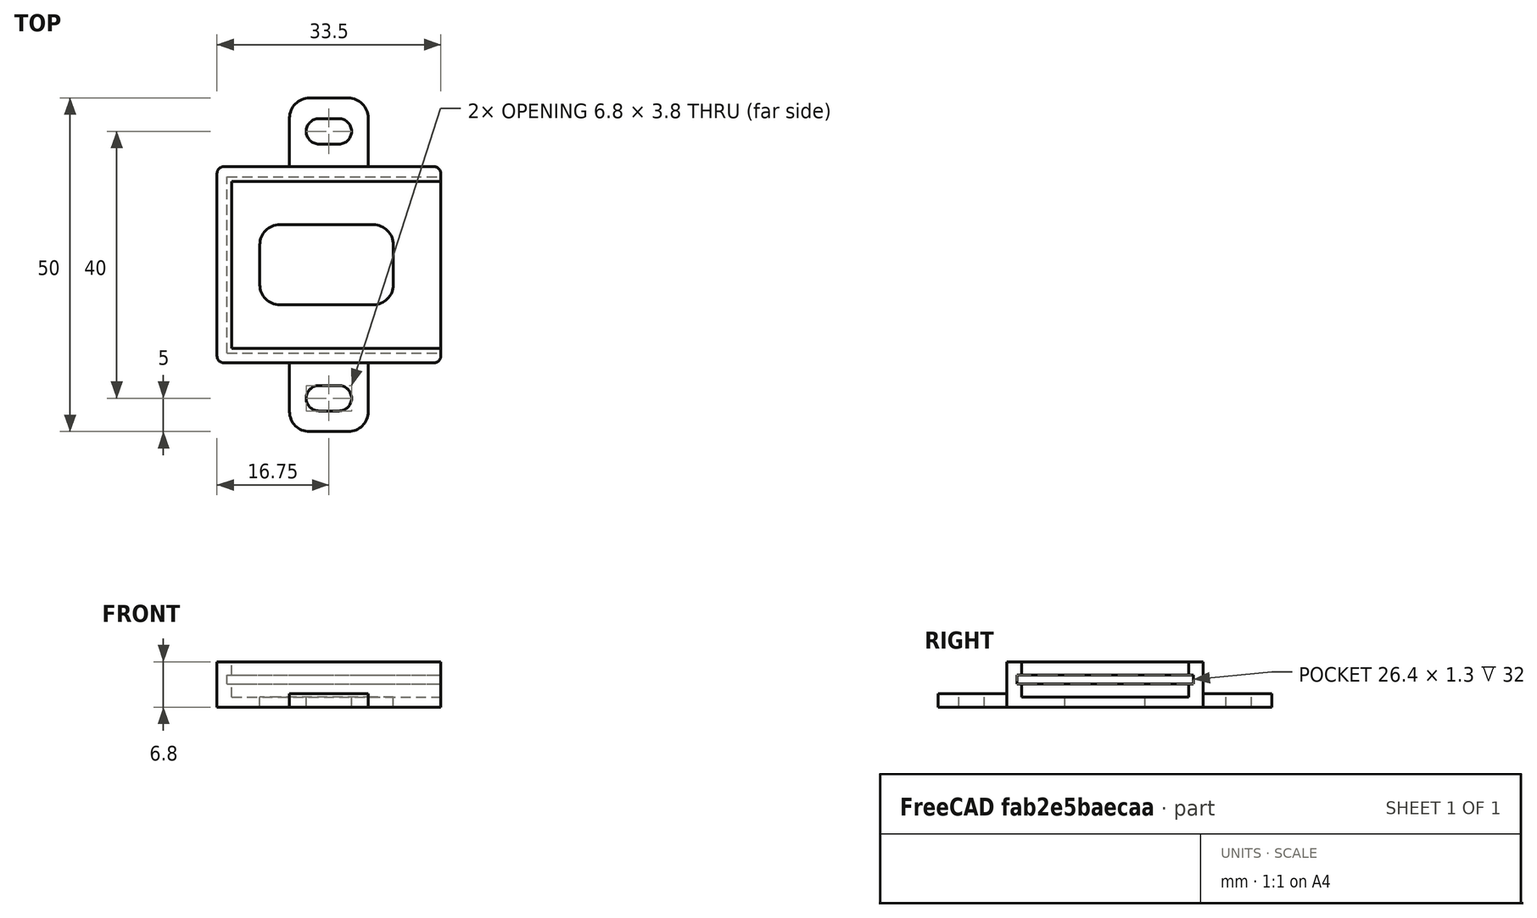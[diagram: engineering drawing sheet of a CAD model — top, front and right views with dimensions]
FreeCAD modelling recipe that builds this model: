
FCSTD DOCUMENT  (FreeCAD 0.19R23578 (Git))
Label: ir_sensor_cheapduino
License: FreeArt
LicenseURL: http://artlibre.org/licence/lal
objects: Part::Box×4, Part::Fillet×2, Part::MultiFuse×2, Spreadsheet::Sheet×1, Part::Feature×1, Part::Cut×1, App::Part×1
note: 10 computed .brp shape members not serialized (recipe doc carries the construction recipe); baked Part::Feature solids carry a one-line shape summary decoded from their .brp

FEATURE [Spreadsheet::Sheet] Spreadsheet  label="p"
  cells = A1=pcb_x; B1(pcb_x)=32; A2=pcb_y; B2(pcb_y)=26.4; A3=pcb_z; B3(pcb_z)=1.3; A4=pcb_under; B4(pcb_under)=2; A5=side_wall; B5(side_wall)=1.5; A6=pcb_side_lane; B6(pcb_side_lane)=0.7; A7=bottom_wall; B7(bottom_wall)=1.5; A8=pcb_above; B8(pcb_above)=2; A9=bottom_hole_x; B9(bottom_hole_x)=20; A10=bottom_hole_y; B10(bottom_hole_y)=12
FEATURE [Part::Box] Box  label="external cube"
  AttacherType = Attacher::AttachEngine3D
  Height = 6.8
  Length = 33.5
  Width = 29.4
  expr: Length = <<p>>.pcb_x + <<p>>.side_wall
  expr: Width = <<p>>.pcb_y + 2 * <<p>>.side_wall
  expr: Height = <<p>>.bottom_wall + <<p>>.pcb_under + <<p>>.pcb_z + <<p>>.pcb_above
FEATURE [Part::Box] Box006  label="internal cube"
  AttacherType = Attacher::AttachEngine3D
  Height = 5.3
  Length = 32.1
  Placement = pos=(2.2,2.2,1.5) rot=(0,0,1;0rad)
  Width = 25
  expr: Length = <<p>>.pcb_x - 2 * <<p>>.pcb_side_lane + <<p>>.side_wall
  expr: Width = <<p>>.pcb_y - 2 * <<p>>.pcb_side_lane
  expr: Height = <<p>>.pcb_under + <<p>>.pcb_z + <<p>>.pcb_above
  expr: .Placement.Base.z = <<p>>.bottom_wall
  expr: .Placement.Base.x = <<p>>.side_wall + <<p>>.pcb_side_lane
  expr: .Placement.Base.y = <<p>>.side_wall + <<p>>.pcb_side_lane
FEATURE [Part::Box] Box007  label="pcb extract cube"
  AttacherType = Attacher::AttachEngine3D
  Height = 1.3
  Length = 32
  Placement = pos=(1.5,1.5,3.5) rot=(0,0,1;0rad)
  Width = 26.4
  expr: Height = <<p>>.pcb_z
  expr: .Placement.Base.z = <<p>>.bottom_wall + <<p>>.pcb_under
  expr: Width = <<p>>.pcb_y
  expr: Length = <<p>>.pcb_x
  expr: .Placement.Base.x = <<p>>.side_wall
  expr: .Placement.Base.y = <<p>>.side_wall
FEATURE [Part::Fillet] Fillet  label="external fillet"
  Base = -> Box
  Edges = 4 edges r=1: [Edge1,Edge3,Edge5,Edge7]
FEATURE [Part::Box] Box008  label="bottom hole"
  AttacherType = Attacher::AttachEngine3D
  Height = 10
  Length = 20
  Placement = pos=(6.4,8.7,0) rot=(0,0,1;0rad)
  Width = 12
  expr: .Placement.Base.y = (<<p>>.pcb_y + 2 * <<p>>.side_wall - <<p>>.bottom_hole_y) / 2
  expr: .Placement.Base.x = (<<p>>.pcb_x + <<p>>.side_wall - <<p>>.pcb_side_lane - <<p>>.bottom_hole_x) / 2
  expr: Width = <<p>>.bottom_hole_y
  expr: Length = <<p>>.bottom_hole_x
FEATURE [Part::Fillet] Fillet001  label="bottom hole fillet"
  Base = -> Box008
  Edges = 4 edges r=3: [Edge1,Edge3,Edge5,Edge7]
FEATURE [Part::MultiFuse] Fusion  label="extract fusion"
  Shapes = -> [Box006,Box007,Fillet001]
FEATURE [Part::Feature] Cut002001  label="attach plane y dir001"
  Placement = pos=(10.85,-10.3,0) rot=(0,0,1;0rad)
  shape: bbox 11.8 x 50 x 2 mm, 20 faces (baked)
FEATURE [Part::MultiFuse] Fusion001  label="solid fusion"
  Shapes = -> [Fillet,Cut002001]
FEATURE [Part::Cut] Cut  label="body cut"
  Base = -> Fusion001
  Tool = -> Fusion
FEATURE [App::Part] Part  label="pcb box part"
  Group = -> [Box,Fillet,Fusion001,Fusion,Box007,Box006,Cut]
  Origin = -> Origin
